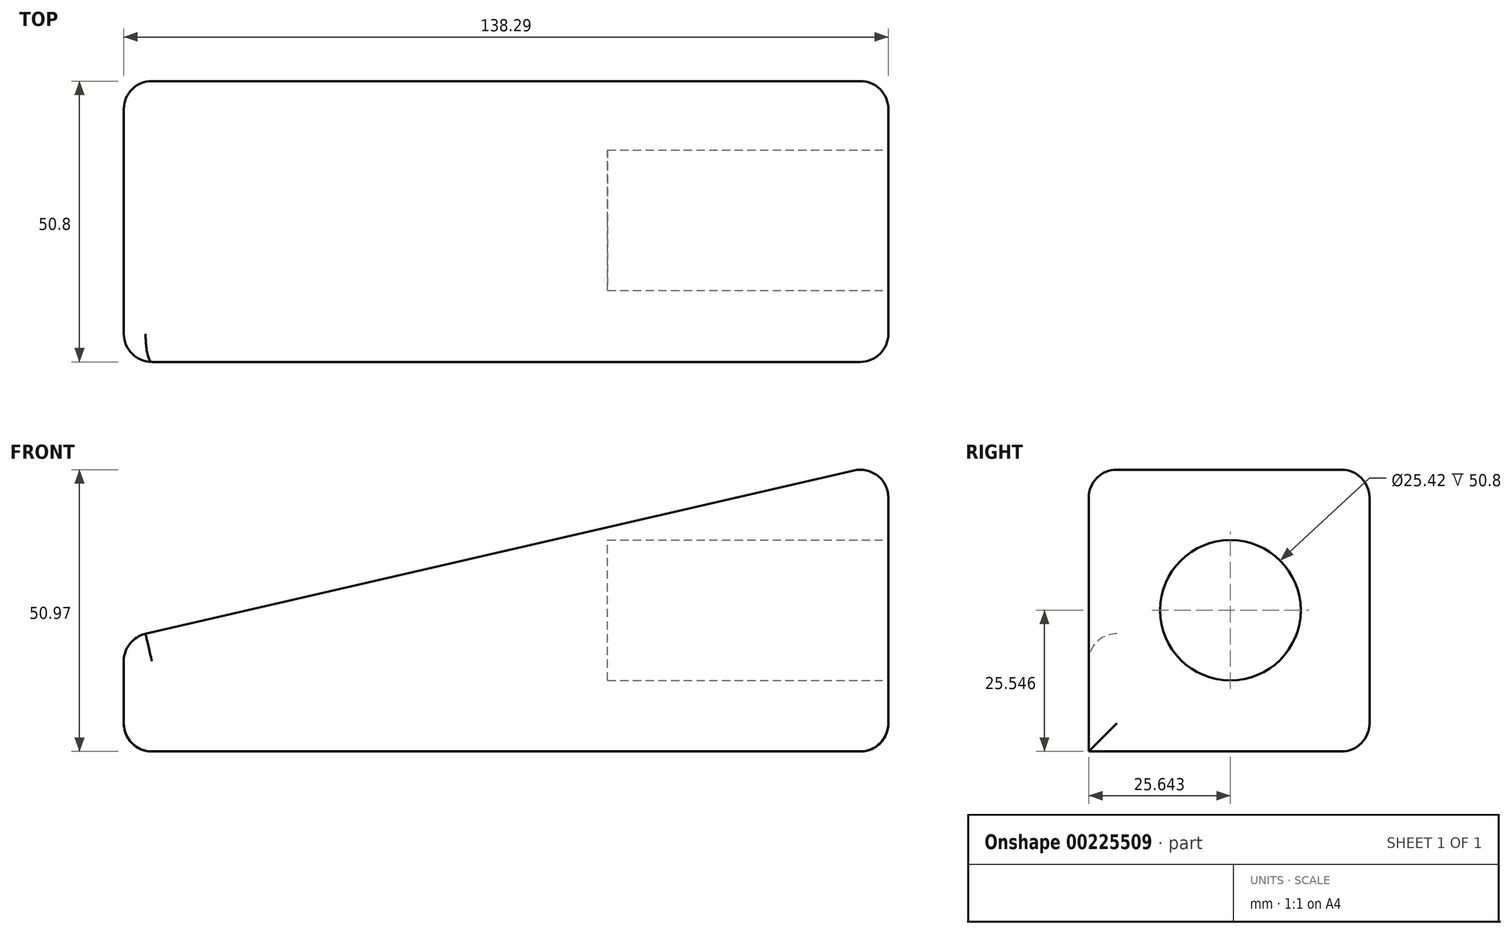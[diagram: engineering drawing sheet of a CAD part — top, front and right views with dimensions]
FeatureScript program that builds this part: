
annotation { "Feature Type Name" : "Feature", "Feature Type Description" : "" }
export const myFeature = defineFeature(function(context is Context, id is Id, definition is map)
    precondition{}
    {
        {
            var Q0;
            Q0=qCreatedBy(makeId("Top.planeOp"),FACE);
            var sketch = newSketch(context, id + "F0", { "sketchPlane" : qUnion([Q0])});
            skSolve(sketch);
        }
        {
            var Q0;
            Q0=qCreatedBy(makeId("Front.planeOp"),FACE);
            var sketch = newSketch(context, id + "F1", { "sketchPlane" : qUnion([Q0])});
            skLineSegment(sketch, "E0", {"start": v(0, 0) * mm, "end": v(75.35, 0) * mm});
            skLineSegment(sketch, "E1", {"start": v(75.35, 0) * mm, "end": v(75.35, 52.27) * mm});
            skLineSegment(sketch, "E2", {"start": v(75.35, 52.27) * mm, "end": v(-62.94, 20.38) * mm});
            skLineSegment(sketch, "E3", {"start": v(-62.94, 20.38) * mm, "end": v(-62.94, 0) * mm});
            skLineSegment(sketch, "E4", {"start": v(-62.94, 0) * mm, "end": v(0, 0) * mm});
            skSolve(sketch);
        }
        {
            var Q0;
            Q0 = qSketchRegion(id + "F0", true);
            var Q1;
            Q1=makeQuery(id+"F1.imprint","IMPRINT",FACE,{"disambiguationData":[TD([[makeQuery(id+"F1.imprint","IMPRINT",EDGE,{"derivedFrom":sQuery(id+"F1.wireOp",EDGE,"E0")}),1.0]])]});
            extrude(context, id + "F2", {"entities" : qUnion([Q0, Q1]), "depth" : 50.8 * mm});
        }
        {
            var Q0;
            Q0=makeQuery(id+"F2.opExtrude","SWEPT_FACE",FACE,{"disambiguationData":[OSD([sQuery(id+"F1.wireOp",EDGE,"E2")])]});
            var Q1;
            Q1=makeQuery(id+"F2.opExtrude","SWEPT_FACE",FACE,{"disambiguationData":[OSD([sQuery(id+"F1.wireOp",EDGE,"E1")])]});
            var Q2;
            Q2=makeQuery(id+"F2.opExtrude","CAP_FACE",FACE,{"disambiguationData":[OSD([sQuery(id+"F1.wireOp",EDGE,"E0"),sQuery(id+"F1.wireOp",EDGE,"E1"),sQuery(id+"F1.wireOp",EDGE,"E2"),sQuery(id+"F1.wireOp",EDGE,"E3"),sQuery(id+"F1.wireOp",EDGE,"E4")])],"isStart":true});
            fillet(context, id + "F3", {"entities" : qUnion([Q0, Q1, Q2]), "radius" : 5.08 * mm, "tangentPropagation" : true, "allowEdgeOverflow" : false});
        }
        {
            var Q0;
            Q0=makeQuery(id+"F2.opExtrude","SWEPT_FACE",FACE,{"disambiguationData":[OSD([sQuery(id+"F1.wireOp",EDGE,"E3")])]});
            fillet(context, id + "F4", {"entities" : qUnion([Q0]), "radius" : 5.08 * mm, "tangentPropagation" : true, "allowEdgeOverflow" : false});
        }
        {
            var Q0;
            Q0=makeQuery(id+"F2.opExtrude","SWEPT_FACE",FACE,{"disambiguationData":[OSD([sQuery(id+"F1.wireOp",EDGE,"E1")])]});
            var sketch = newSketch(context, id + "F5", { "sketchPlane" : qUnion([Q0])});
            skCircle(sketch, "E5", {"center": v(-25.16, 25.55) * mm, "radius": 12.71 * mm});
            skSolve(sketch);
        }
        {
            var Q0;
            Q0=makeQuery(id+"F5.imprint","IMPRINT",FACE,{"disambiguationData":[TD([[makeQuery(id+"F5.imprint","IMPRINT",EDGE,{"derivedFrom":sQuery(id+"F5.wireOp",EDGE,"E5")}),1.0]])]});
            var Q1;
            Q1=sQuery(id+"F5.wireOp",EDGE,"E5");
            extrude(context, id + "F6", {"entities" : qUnion([Q0]), "operationType" : NewBodyOperationType.REMOVE, "surfaceEntities" : qUnion([Q1]), "oppositeDirection" : true, "depth" : 50.8 * mm});
        }
    });
